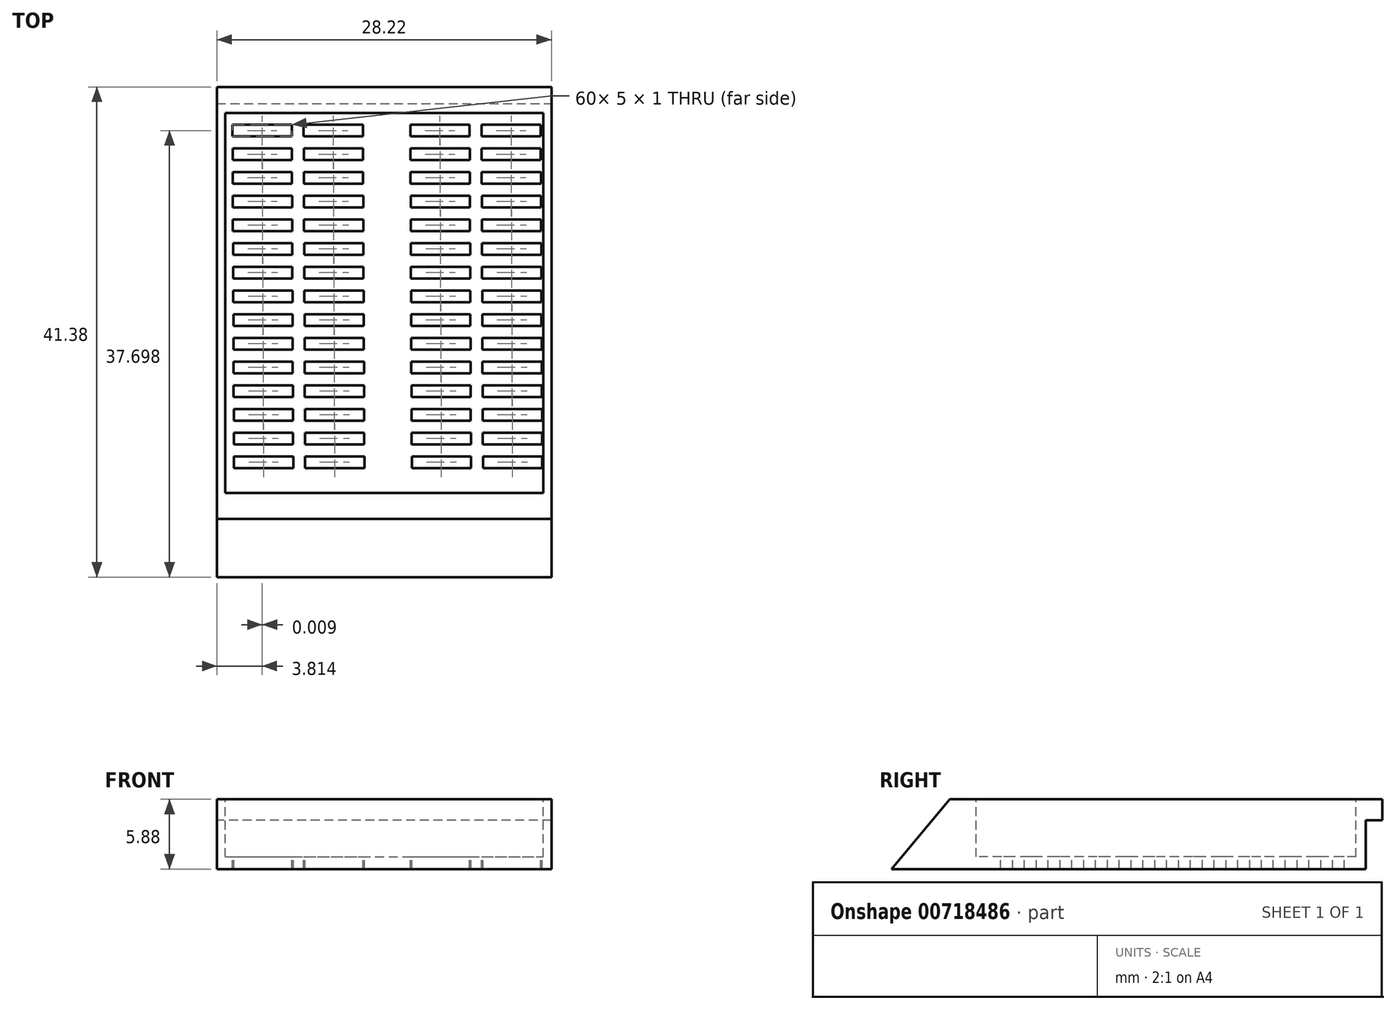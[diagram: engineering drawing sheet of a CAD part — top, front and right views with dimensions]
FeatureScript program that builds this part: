
annotation { "Feature Type Name" : "Feature", "Feature Type Description" : "" }
export const myFeature = defineFeature(function(context is Context, id is Id, definition is map)
    precondition{}
    {
        {
            var Q0;
            Q0=qCreatedBy(makeId("Top.planeOp"),FACE);
            var sketch = newSketch(context, id + "F0", { "sketchPlane" : qUnion([Q0])});
            skLineSegment(sketch, "E0.bottom", {"start": v(-12.14, 10.35) * mm, "end": v(16.08, 10.35) * mm});
            skLineSegment(sketch, "E0.top", {"start": v(-12.14, -29.63) * mm, "end": v(16.08, -29.63) * mm});
            skLineSegment(sketch, "E0.left", {"start": v(-12.14, 10.35) * mm, "end": v(-12.14, -29.63) * mm});
            skLineSegment(sketch, "E0.right", {"start": v(16.08, 10.35) * mm, "end": v(16.08, -29.63) * mm});
            skSolve(sketch);
        }
        {
            var Q0;
            Q0 = qSketchRegion(id + "F0", true);
            extrude(context, id + "F1", {"entities" : qUnion([Q0]), "depth" : 5.88 * mm, "offsetDistance" : 25.4 * mm});
        }
        {
            var Q0;
            Q0=makeQuery(id+"F1.opExtrude","SWEPT_FACE",FACE,{"disambiguationData":[OSD([sQuery(id+"F0.wireOp",EDGE,"E0.left")])]});
            var sketch = newSketch(context, id + "F2", { "sketchPlane" : qUnion([Q0])});
            skLineSegment(sketch, "E1", {"start": v(29.63, 0) * mm, "end": v(24.7, 0) * mm});
            skLineSegment(sketch, "E2", {"start": v(24.7, 0) * mm, "end": v(24.7, 5.88) * mm});
            skLineSegment(sketch, "E3", {"start": v(24.7, 5.88) * mm, "end": v(29.63, 0) * mm});
            skLineSegment(sketch, "E4", {"start": v(29.63, 0) * mm, "end": v(29.63, 5.88) * mm});
            skLineSegment(sketch, "E5", {"start": v(29.63, 5.88) * mm, "end": v(24.7, 5.88) * mm});
            skSolve(sketch);
        }
        {
            var Q0;
            Q0=makeQuery(id+"F2.imprint","IMPRINT",FACE,{"disambiguationData":[TD([[makeQuery(id+"F2.imprint","IMPRINT",EDGE,{"derivedFrom":sQuery(id+"F2.wireOp",EDGE,"E3")}),1.0]])]});
            extrude(context, id + "F3", {"entities" : qUnion([Q0]), "operationType" : NewBodyOperationType.REMOVE, "endBound" : BoundingType.UP_TO_NEXT, "oppositeDirection" : true, "depth" : 25.4 * mm, "offsetDistance" : 25.4 * mm});
        }
        {
            var Q0;
            Q0=makeQuery(id+"F1.opExtrude","SWEPT_FACE",FACE,{"disambiguationData":[OSD([sQuery(id+"F0.wireOp",EDGE,"E0.bottom")])]});
            var sketch = newSketch(context, id + "F4", { "sketchPlane" : qUnion([Q0])});
            skLineSegment(sketch, "E6.bottom", {"start": v(-16.08, 5.88) * mm, "end": v(12.14, 5.88) * mm});
            skLineSegment(sketch, "E6.top", {"start": v(-16.08, 4.13) * mm, "end": v(12.14, 4.13) * mm});
            skLineSegment(sketch, "E6.left", {"start": v(-16.08, 5.88) * mm, "end": v(-16.08, 4.13) * mm});
            skLineSegment(sketch, "E6.right", {"start": v(12.14, 5.88) * mm, "end": v(12.14, 4.13) * mm});
            skSolve(sketch);
        }
        {
            var Q0;
            Q0=makeQuery(id+"F4.imprint","IMPRINT",FACE,{"disambiguationData":[TD([[makeQuery(id+"F4.imprint","IMPRINT",EDGE,{"derivedFrom":sQuery(id+"F4.wireOp",EDGE,"E6.bottom")}),1.0]])]});
            extrude(context, id + "F5", {"entities" : qUnion([Q0]), "operationType" : NewBodyOperationType.ADD, "depth" : 1.4 * mm, "offsetDistance" : 25.4 * mm});
        }
        {
            var Q0;
            Q0=makeQuery(id+"F5.boolean.opBoolean","MERGE",FACE,{"derivedFrom":[makeQuery(id+"F1.opExtrude","CAP_FACE",FACE,{"disambiguationData":[OSD([sQuery(id+"F0.wireOp",EDGE,"E0.bottom"),sQuery(id+"F0.wireOp",EDGE,"E0.top"),sQuery(id+"F0.wireOp",EDGE,"E0.left"),sQuery(id+"F0.wireOp",EDGE,"E0.right")])],"isStart":false}),makeQuery(id+"F5.opExtrude","SWEPT_FACE",FACE,{"disambiguationData":[OSD([sQuery(id+"F4.wireOp",EDGE,"E6.bottom")])]})]});
            var sketch = newSketch(context, id + "F6", { "sketchPlane" : qUnion([Q0])});
            skLineSegment(sketch, "E7.bottom", {"start": v(-11.44, 9.55) * mm, "end": v(15.38, 9.55) * mm});
            skLineSegment(sketch, "E7.top", {"start": v(-11.44, -22.5) * mm, "end": v(15.38, -22.5) * mm});
            skLineSegment(sketch, "E7.left", {"start": v(-11.44, 9.55) * mm, "end": v(-11.44, -22.5) * mm});
            skLineSegment(sketch, "E7.right", {"start": v(15.38, 9.55) * mm, "end": v(15.38, -22.5) * mm});
            skLineSegment(sketch, "E8", {"start": v(-11.44, -6.48) * mm, "end": v(-12.14, -6.48) * mm});
            skLineSegment(sketch, "E9", {"start": v(15.38, -6.48) * mm, "end": v(16.08, -6.48) * mm});
            skLineSegment(sketch, "E10", {"start": v(15.38, -22.5) * mm, "end": v(15.38, -24.7) * mm});
            skLineSegment(sketch, "E11", {"start": v(13.6, 9.55) * mm, "end": v(13.6, 11.75) * mm});
            skSolve(sketch);
        }
        {
            var Q0;
            {var subQ4=sQuery(id+"F6.wireOp",EDGE,"E7.top");Q0=makeQuery(id+"F6.imprint","IMPRINT",FACE,{"disambiguationData":[TD([[makeQuery(id+"F6.imprint","IMPRINT",EDGE,{"derivedFrom":subQ4}),1.0]])]});}
            extrude(context, id + "F7", {"entities" : qUnion([Q0]), "operationType" : NewBodyOperationType.REMOVE, "oppositeDirection" : true, "depth" : 4.85 * mm, "offsetDistance" : 25.4 * mm});
        }
        {
            var Q0;
            {var subQ4=sQuery(id+"F6.wireOp",EDGE,"E7.top");Q0=makeQuery(id+"F6.imprint","IMPRINT",FACE,{"disambiguationData":[TD([[makeQuery(id+"F6.imprint","IMPRINT",EDGE,{"derivedFrom":subQ4}),1.0]])]});}
            var sketch = newSketch(context, id + "F8", { "sketchPlane" : qUnion([Q0])});
            skLineSegment(sketch, "E12.bottom", {"start": v(-10.83, 8.57) * mm, "end": v(-5.83, 8.57) * mm});
            skLineSegment(sketch, "E12.top", {"start": v(-10.83, 7.57) * mm, "end": v(-5.83, 7.57) * mm});
            skLineSegment(sketch, "E12.left", {"start": v(-10.83, 8.57) * mm, "end": v(-10.83, 7.57) * mm});
            skLineSegment(sketch, "E12.right", {"start": v(-5.83, 8.57) * mm, "end": v(-5.83, 7.57) * mm});
            skLineSegment(sketch, "E13", {"start": v(-10.83, 8.57) * mm, "end": v(-10.83, 9.57) * mm});
            skLineSegment(sketch, "E14.1.0.0", {"start": v(-4.83, 8.57) * mm, "end": v(0.17, 8.57) * mm});
            skLineSegment(sketch, "E14.1.0.1", {"start": v(-4.83, 7.57) * mm, "end": v(0.17, 7.57) * mm});
            skLineSegment(sketch, "E14.1.0.2", {"start": v(0.17, 8.57) * mm, "end": v(0.17, 7.57) * mm});
            skLineSegment(sketch, "E14.1.0.3", {"start": v(-4.83, 8.57) * mm, "end": v(-4.83, 7.57) * mm});
            skLineSegment(sketch, "E14.direction1", {"start": v(-10.83, 7.57) * mm, "end": v(-4.83, 7.57) * mm, "construction": true});
            skLineSegment(sketch, "E15.1.0.0", {"start": v(10.17, 8.57) * mm, "end": v(10.17, 7.57) * mm});
            skLineSegment(sketch, "E15.1.0.1", {"start": v(15.17, 8.57) * mm, "end": v(15.17, 7.57) * mm});
            skLineSegment(sketch, "E15.1.0.2", {"start": v(10.17, 7.57) * mm, "end": v(15.17, 7.57) * mm});
            skLineSegment(sketch, "E15.1.0.3", {"start": v(10.17, 8.57) * mm, "end": v(15.17, 8.57) * mm});
            skLineSegment(sketch, "E15.1.0.4", {"start": v(4.17, 8.57) * mm, "end": v(9.17, 8.57) * mm});
            skLineSegment(sketch, "E15.1.0.5", {"start": v(9.17, 8.57) * mm, "end": v(9.17, 7.57) * mm});
            skLineSegment(sketch, "E15.1.0.6", {"start": v(4.17, 7.57) * mm, "end": v(10.17, 7.57) * mm, "construction": true});
            skLineSegment(sketch, "E15.1.0.7", {"start": v(4.17, 8.57) * mm, "end": v(4.17, 7.57) * mm});
            skLineSegment(sketch, "E15.1.0.8", {"start": v(4.17, 7.57) * mm, "end": v(9.17, 7.57) * mm});
            skLineSegment(sketch, "E15.direction1", {"start": v(-10.83, 7.57) * mm, "end": v(4.17, 7.57) * mm, "construction": true});
            skLineSegment(sketch, "E16.1.0.0", {"start": v(4.18, 5.57) * mm, "end": v(10.18, 5.57) * mm, "construction": true});
            skLineSegment(sketch, "E16.1.0.1", {"start": v(-4.82, 6.57) * mm, "end": v(0.18, 6.57) * mm});
            skLineSegment(sketch, "E16.1.0.2", {"start": v(10.18, 6.57) * mm, "end": v(15.18, 6.57) * mm});
            skLineSegment(sketch, "E16.1.0.3", {"start": v(4.18, 6.57) * mm, "end": v(9.18, 6.57) * mm});
            skLineSegment(sketch, "E16.1.0.4", {"start": v(9.18, 6.57) * mm, "end": v(9.18, 5.57) * mm});
            skLineSegment(sketch, "E16.1.0.5", {"start": v(-5.82, 6.57) * mm, "end": v(-5.82, 5.57) * mm});
            skLineSegment(sketch, "E16.1.0.6", {"start": v(-10.82, 6.57) * mm, "end": v(-5.82, 6.57) * mm});
            skLineSegment(sketch, "E16.1.0.7", {"start": v(-10.82, 6.57) * mm, "end": v(-10.82, 5.57) * mm});
            skLineSegment(sketch, "E16.1.0.8", {"start": v(0.18, 6.57) * mm, "end": v(0.18, 5.57) * mm});
            skLineSegment(sketch, "E16.1.0.9", {"start": v(-4.82, 6.57) * mm, "end": v(-4.82, 5.57) * mm});
            skLineSegment(sketch, "E16.1.0.10", {"start": v(10.18, 6.57) * mm, "end": v(10.18, 5.57) * mm});
            skLineSegment(sketch, "E16.1.0.11", {"start": v(4.18, 6.57) * mm, "end": v(4.18, 5.57) * mm});
            skLineSegment(sketch, "E16.1.0.12", {"start": v(15.18, 6.57) * mm, "end": v(15.18, 5.57) * mm});
            skLineSegment(sketch, "E16.1.0.13", {"start": v(10.18, 5.57) * mm, "end": v(15.18, 5.57) * mm});
            skLineSegment(sketch, "E16.1.0.14", {"start": v(-10.82, 5.57) * mm, "end": v(4.18, 5.57) * mm, "construction": true});
            skLineSegment(sketch, "E16.1.0.15", {"start": v(-4.82, 5.57) * mm, "end": v(0.18, 5.57) * mm});
            skLineSegment(sketch, "E16.1.0.16", {"start": v(4.18, 5.57) * mm, "end": v(9.18, 5.57) * mm});
            skLineSegment(sketch, "E16.1.0.17", {"start": v(-10.82, 5.57) * mm, "end": v(-4.82, 5.57) * mm, "construction": true});
            skLineSegment(sketch, "E16.1.0.18", {"start": v(-10.82, 5.57) * mm, "end": v(-5.82, 5.57) * mm});
            skLineSegment(sketch, "E16.2.0.0", {"start": v(4.2, 3.57) * mm, "end": v(10.2, 3.57) * mm, "construction": true});
            skLineSegment(sketch, "E16.2.0.1", {"start": v(-4.8, 4.57) * mm, "end": v(0.2, 4.57) * mm});
            skLineSegment(sketch, "E16.2.0.2", {"start": v(10.2, 4.57) * mm, "end": v(15.2, 4.57) * mm});
            skLineSegment(sketch, "E16.2.0.3", {"start": v(4.2, 4.57) * mm, "end": v(9.2, 4.57) * mm});
            skLineSegment(sketch, "E16.2.0.4", {"start": v(9.2, 4.57) * mm, "end": v(9.2, 3.57) * mm});
            skLineSegment(sketch, "E16.2.0.5", {"start": v(-5.8, 4.57) * mm, "end": v(-5.8, 3.57) * mm});
            skLineSegment(sketch, "E16.2.0.6", {"start": v(-10.8, 4.57) * mm, "end": v(-5.8, 4.57) * mm});
            skLineSegment(sketch, "E16.2.0.7", {"start": v(-10.8, 4.57) * mm, "end": v(-10.8, 3.57) * mm});
            skLineSegment(sketch, "E16.2.0.8", {"start": v(0.2, 4.57) * mm, "end": v(0.2, 3.57) * mm});
            skLineSegment(sketch, "E16.2.0.9", {"start": v(-4.8, 4.57) * mm, "end": v(-4.8, 3.57) * mm});
            skLineSegment(sketch, "E16.2.0.10", {"start": v(10.2, 4.57) * mm, "end": v(10.2, 3.57) * mm});
            skLineSegment(sketch, "E16.2.0.11", {"start": v(4.2, 4.57) * mm, "end": v(4.2, 3.57) * mm});
            skLineSegment(sketch, "E16.2.0.12", {"start": v(15.2, 4.57) * mm, "end": v(15.2, 3.57) * mm});
            skLineSegment(sketch, "E16.2.0.13", {"start": v(10.2, 3.57) * mm, "end": v(15.2, 3.57) * mm});
            skLineSegment(sketch, "E16.2.0.14", {"start": v(-10.8, 3.57) * mm, "end": v(4.2, 3.57) * mm, "construction": true});
            skLineSegment(sketch, "E16.2.0.15", {"start": v(-4.8, 3.57) * mm, "end": v(0.2, 3.57) * mm});
            skLineSegment(sketch, "E16.2.0.16", {"start": v(4.2, 3.57) * mm, "end": v(9.2, 3.57) * mm});
            skLineSegment(sketch, "E16.2.0.17", {"start": v(-10.8, 3.57) * mm, "end": v(-4.8, 3.57) * mm, "construction": true});
            skLineSegment(sketch, "E16.2.0.18", {"start": v(-10.8, 3.57) * mm, "end": v(-5.8, 3.57) * mm});
            skLineSegment(sketch, "E16.3.0.0", {"start": v(4.2, 1.57) * mm, "end": v(10.2, 1.57) * mm, "construction": true});
            skLineSegment(sketch, "E16.3.0.1", {"start": v(-4.8, 2.57) * mm, "end": v(0.2, 2.57) * mm});
            skLineSegment(sketch, "E16.3.0.2", {"start": v(10.2, 2.57) * mm, "end": v(15.2, 2.57) * mm});
            skLineSegment(sketch, "E16.3.0.3", {"start": v(4.2, 2.57) * mm, "end": v(9.2, 2.57) * mm});
            skLineSegment(sketch, "E16.3.0.4", {"start": v(9.2, 2.57) * mm, "end": v(9.2, 1.57) * mm});
            skLineSegment(sketch, "E16.3.0.5", {"start": v(-5.8, 2.57) * mm, "end": v(-5.8, 1.57) * mm});
            skLineSegment(sketch, "E16.3.0.6", {"start": v(-10.8, 2.57) * mm, "end": v(-5.8, 2.57) * mm});
            skLineSegment(sketch, "E16.3.0.7", {"start": v(-10.8, 2.57) * mm, "end": v(-10.8, 1.57) * mm});
            skLineSegment(sketch, "E16.3.0.8", {"start": v(0.2, 2.57) * mm, "end": v(0.2, 1.57) * mm});
            skLineSegment(sketch, "E16.3.0.9", {"start": v(-4.8, 2.57) * mm, "end": v(-4.8, 1.57) * mm});
            skLineSegment(sketch, "E16.3.0.10", {"start": v(10.2, 2.57) * mm, "end": v(10.2, 1.57) * mm});
            skLineSegment(sketch, "E16.3.0.11", {"start": v(4.2, 2.57) * mm, "end": v(4.2, 1.57) * mm});
            skLineSegment(sketch, "E16.3.0.12", {"start": v(15.2, 2.57) * mm, "end": v(15.2, 1.57) * mm});
            skLineSegment(sketch, "E16.3.0.13", {"start": v(10.2, 1.57) * mm, "end": v(15.2, 1.57) * mm});
            skLineSegment(sketch, "E16.3.0.14", {"start": v(-10.8, 1.57) * mm, "end": v(4.2, 1.57) * mm, "construction": true});
            skLineSegment(sketch, "E16.3.0.15", {"start": v(-4.8, 1.57) * mm, "end": v(0.2, 1.57) * mm});
            skLineSegment(sketch, "E16.3.0.16", {"start": v(4.2, 1.57) * mm, "end": v(9.2, 1.57) * mm});
            skLineSegment(sketch, "E16.3.0.17", {"start": v(-10.8, 1.57) * mm, "end": v(-4.8, 1.57) * mm, "construction": true});
            skLineSegment(sketch, "E16.3.0.18", {"start": v(-10.8, 1.57) * mm, "end": v(-5.8, 1.57) * mm});
            skLineSegment(sketch, "E16.4.0.0", {"start": v(4.2, -0.43) * mm, "end": v(10.2, -0.43) * mm, "construction": true});
            skLineSegment(sketch, "E16.4.0.1", {"start": v(-4.8, 0.57) * mm, "end": v(0.2, 0.57) * mm});
            skLineSegment(sketch, "E16.4.0.2", {"start": v(10.2, 0.57) * mm, "end": v(15.2, 0.57) * mm});
            skLineSegment(sketch, "E16.4.0.3", {"start": v(4.2, 0.57) * mm, "end": v(9.2, 0.57) * mm});
            skLineSegment(sketch, "E16.4.0.4", {"start": v(9.2, 0.57) * mm, "end": v(9.2, -0.43) * mm});
            skLineSegment(sketch, "E16.4.0.5", {"start": v(-5.8, 0.57) * mm, "end": v(-5.8, -0.43) * mm});
            skLineSegment(sketch, "E16.4.0.6", {"start": v(-10.8, 0.57) * mm, "end": v(-5.8, 0.57) * mm});
            skLineSegment(sketch, "E16.4.0.7", {"start": v(-10.8, 0.57) * mm, "end": v(-10.8, -0.43) * mm});
            skLineSegment(sketch, "E16.4.0.8", {"start": v(0.2, 0.57) * mm, "end": v(0.2, -0.43) * mm});
            skLineSegment(sketch, "E16.4.0.9", {"start": v(-4.8, 0.57) * mm, "end": v(-4.8, -0.43) * mm});
            skLineSegment(sketch, "E16.4.0.10", {"start": v(10.2, 0.57) * mm, "end": v(10.2, -0.43) * mm});
            skLineSegment(sketch, "E16.4.0.11", {"start": v(4.2, 0.57) * mm, "end": v(4.2, -0.43) * mm});
            skLineSegment(sketch, "E16.4.0.12", {"start": v(15.2, 0.57) * mm, "end": v(15.2, -0.43) * mm});
            skLineSegment(sketch, "E16.4.0.13", {"start": v(10.2, -0.43) * mm, "end": v(15.2, -0.43) * mm});
            skLineSegment(sketch, "E16.4.0.14", {"start": v(-10.8, -0.43) * mm, "end": v(4.2, -0.43) * mm, "construction": true});
            skLineSegment(sketch, "E16.4.0.15", {"start": v(-4.8, -0.43) * mm, "end": v(0.2, -0.43) * mm});
            skLineSegment(sketch, "E16.4.0.16", {"start": v(4.2, -0.43) * mm, "end": v(9.2, -0.43) * mm});
            skLineSegment(sketch, "E16.4.0.17", {"start": v(-10.8, -0.43) * mm, "end": v(-4.8, -0.43) * mm, "construction": true});
            skLineSegment(sketch, "E16.4.0.18", {"start": v(-10.8, -0.43) * mm, "end": v(-5.8, -0.43) * mm});
            skLineSegment(sketch, "E16.5.0.0", {"start": v(4.22, -2.43) * mm, "end": v(10.22, -2.43) * mm, "construction": true});
            skLineSegment(sketch, "E16.5.0.1", {"start": v(-4.78, -1.43) * mm, "end": v(0.22, -1.43) * mm});
            skLineSegment(sketch, "E16.5.0.2", {"start": v(10.22, -1.43) * mm, "end": v(15.22, -1.43) * mm});
            skLineSegment(sketch, "E16.5.0.3", {"start": v(4.22, -1.43) * mm, "end": v(9.22, -1.43) * mm});
            skLineSegment(sketch, "E16.5.0.4", {"start": v(9.22, -1.43) * mm, "end": v(9.22, -2.43) * mm});
            skLineSegment(sketch, "E16.5.0.5", {"start": v(-5.78, -1.43) * mm, "end": v(-5.78, -2.43) * mm});
            skLineSegment(sketch, "E16.5.0.6", {"start": v(-10.78, -1.43) * mm, "end": v(-5.78, -1.43) * mm});
            skLineSegment(sketch, "E16.5.0.7", {"start": v(-10.78, -1.43) * mm, "end": v(-10.78, -2.43) * mm});
            skLineSegment(sketch, "E16.5.0.8", {"start": v(0.22, -1.43) * mm, "end": v(0.22, -2.43) * mm});
            skLineSegment(sketch, "E16.5.0.9", {"start": v(-4.78, -1.43) * mm, "end": v(-4.78, -2.43) * mm});
            skLineSegment(sketch, "E16.5.0.10", {"start": v(10.22, -1.43) * mm, "end": v(10.22, -2.43) * mm});
            skLineSegment(sketch, "E16.5.0.11", {"start": v(4.22, -1.43) * mm, "end": v(4.22, -2.43) * mm});
            skLineSegment(sketch, "E16.5.0.12", {"start": v(15.22, -1.43) * mm, "end": v(15.22, -2.43) * mm});
            skLineSegment(sketch, "E16.5.0.13", {"start": v(10.22, -2.43) * mm, "end": v(15.22, -2.43) * mm});
            skLineSegment(sketch, "E16.5.0.14", {"start": v(-10.78, -2.43) * mm, "end": v(4.22, -2.43) * mm, "construction": true});
            skLineSegment(sketch, "E16.5.0.15", {"start": v(-4.78, -2.43) * mm, "end": v(0.22, -2.43) * mm});
            skLineSegment(sketch, "E16.5.0.16", {"start": v(4.22, -2.43) * mm, "end": v(9.22, -2.43) * mm});
            skLineSegment(sketch, "E16.5.0.17", {"start": v(-10.78, -2.43) * mm, "end": v(-4.78, -2.43) * mm, "construction": true});
            skLineSegment(sketch, "E16.5.0.18", {"start": v(-10.78, -2.43) * mm, "end": v(-5.78, -2.43) * mm});
            skLineSegment(sketch, "E16.6.0.0", {"start": v(4.23, -4.43) * mm, "end": v(10.23, -4.43) * mm, "construction": true});
            skLineSegment(sketch, "E16.6.0.1", {"start": v(-4.77, -3.43) * mm, "end": v(0.23, -3.43) * mm});
            skLineSegment(sketch, "E16.6.0.2", {"start": v(10.23, -3.43) * mm, "end": v(15.23, -3.43) * mm});
            skLineSegment(sketch, "E16.6.0.3", {"start": v(4.23, -3.43) * mm, "end": v(9.23, -3.43) * mm});
            skLineSegment(sketch, "E16.6.0.4", {"start": v(9.23, -3.43) * mm, "end": v(9.23, -4.43) * mm});
            skLineSegment(sketch, "E16.6.0.5", {"start": v(-5.77, -3.43) * mm, "end": v(-5.77, -4.43) * mm});
            skLineSegment(sketch, "E16.6.0.6", {"start": v(-10.77, -3.43) * mm, "end": v(-5.77, -3.43) * mm});
            skLineSegment(sketch, "E16.6.0.7", {"start": v(-10.77, -3.43) * mm, "end": v(-10.77, -4.43) * mm});
            skLineSegment(sketch, "E16.6.0.8", {"start": v(0.23, -3.43) * mm, "end": v(0.23, -4.43) * mm});
            skLineSegment(sketch, "E16.6.0.9", {"start": v(-4.77, -3.43) * mm, "end": v(-4.77, -4.43) * mm});
            skLineSegment(sketch, "E16.6.0.10", {"start": v(10.23, -3.43) * mm, "end": v(10.23, -4.43) * mm});
            skLineSegment(sketch, "E16.6.0.11", {"start": v(4.23, -3.43) * mm, "end": v(4.23, -4.43) * mm});
            skLineSegment(sketch, "E16.6.0.12", {"start": v(15.23, -3.43) * mm, "end": v(15.23, -4.43) * mm});
            skLineSegment(sketch, "E16.6.0.13", {"start": v(10.23, -4.43) * mm, "end": v(15.23, -4.43) * mm});
            skLineSegment(sketch, "E16.6.0.14", {"start": v(-10.77, -4.43) * mm, "end": v(4.23, -4.43) * mm, "construction": true});
            skLineSegment(sketch, "E16.6.0.15", {"start": v(-4.77, -4.43) * mm, "end": v(0.23, -4.43) * mm});
            skLineSegment(sketch, "E16.6.0.16", {"start": v(4.23, -4.43) * mm, "end": v(9.23, -4.43) * mm});
            skLineSegment(sketch, "E16.6.0.17", {"start": v(-10.77, -4.43) * mm, "end": v(-4.77, -4.43) * mm, "construction": true});
            skLineSegment(sketch, "E16.6.0.18", {"start": v(-10.77, -4.43) * mm, "end": v(-5.77, -4.43) * mm});
            skLineSegment(sketch, "E16.7.0.0", {"start": v(4.23, -6.43) * mm, "end": v(10.23, -6.43) * mm, "construction": true});
            skLineSegment(sketch, "E16.7.0.1", {"start": v(-4.77, -5.43) * mm, "end": v(0.23, -5.43) * mm});
            skLineSegment(sketch, "E16.7.0.2", {"start": v(10.23, -5.43) * mm, "end": v(15.23, -5.43) * mm});
            skLineSegment(sketch, "E16.7.0.3", {"start": v(4.23, -5.43) * mm, "end": v(9.23, -5.43) * mm});
            skLineSegment(sketch, "E16.7.0.4", {"start": v(9.23, -5.43) * mm, "end": v(9.23, -6.43) * mm});
            skLineSegment(sketch, "E16.7.0.5", {"start": v(-5.77, -5.43) * mm, "end": v(-5.77, -6.43) * mm});
            skLineSegment(sketch, "E16.7.0.6", {"start": v(-10.77, -5.43) * mm, "end": v(-5.77, -5.43) * mm});
            skLineSegment(sketch, "E16.7.0.7", {"start": v(-10.77, -5.43) * mm, "end": v(-10.77, -6.43) * mm});
            skLineSegment(sketch, "E16.7.0.8", {"start": v(0.23, -5.43) * mm, "end": v(0.23, -6.43) * mm});
            skLineSegment(sketch, "E16.7.0.9", {"start": v(-4.77, -5.43) * mm, "end": v(-4.77, -6.43) * mm});
            skLineSegment(sketch, "E16.7.0.10", {"start": v(10.23, -5.43) * mm, "end": v(10.23, -6.43) * mm});
            skLineSegment(sketch, "E16.7.0.11", {"start": v(4.23, -5.43) * mm, "end": v(4.23, -6.43) * mm});
            skLineSegment(sketch, "E16.7.0.12", {"start": v(15.23, -5.43) * mm, "end": v(15.23, -6.43) * mm});
            skLineSegment(sketch, "E16.7.0.13", {"start": v(10.23, -6.43) * mm, "end": v(15.23, -6.43) * mm});
            skLineSegment(sketch, "E16.7.0.14", {"start": v(-10.77, -6.43) * mm, "end": v(4.23, -6.43) * mm, "construction": true});
            skLineSegment(sketch, "E16.7.0.15", {"start": v(-4.77, -6.43) * mm, "end": v(0.23, -6.43) * mm});
            skLineSegment(sketch, "E16.7.0.16", {"start": v(4.23, -6.43) * mm, "end": v(9.23, -6.43) * mm});
            skLineSegment(sketch, "E16.7.0.17", {"start": v(-10.77, -6.43) * mm, "end": v(-4.77, -6.43) * mm, "construction": true});
            skLineSegment(sketch, "E16.7.0.18", {"start": v(-10.77, -6.43) * mm, "end": v(-5.77, -6.43) * mm});
            skLineSegment(sketch, "E16.8.0.0", {"start": v(4.24, -8.43) * mm, "end": v(10.24, -8.43) * mm, "construction": true});
            skLineSegment(sketch, "E16.8.0.1", {"start": v(-4.76, -7.43) * mm, "end": v(0.24, -7.43) * mm});
            skLineSegment(sketch, "E16.8.0.2", {"start": v(10.24, -7.43) * mm, "end": v(15.24, -7.43) * mm});
            skLineSegment(sketch, "E16.8.0.3", {"start": v(4.24, -7.43) * mm, "end": v(9.24, -7.43) * mm});
            skLineSegment(sketch, "E16.8.0.4", {"start": v(9.24, -7.43) * mm, "end": v(9.24, -8.43) * mm});
            skLineSegment(sketch, "E16.8.0.5", {"start": v(-5.76, -7.43) * mm, "end": v(-5.76, -8.43) * mm});
            skLineSegment(sketch, "E16.8.0.6", {"start": v(-10.76, -7.43) * mm, "end": v(-5.76, -7.43) * mm});
            skLineSegment(sketch, "E16.8.0.7", {"start": v(-10.76, -7.43) * mm, "end": v(-10.76, -8.43) * mm});
            skLineSegment(sketch, "E16.8.0.8", {"start": v(0.24, -7.43) * mm, "end": v(0.24, -8.43) * mm});
            skLineSegment(sketch, "E16.8.0.9", {"start": v(-4.76, -7.43) * mm, "end": v(-4.76, -8.43) * mm});
            skLineSegment(sketch, "E16.8.0.10", {"start": v(10.24, -7.43) * mm, "end": v(10.24, -8.43) * mm});
            skLineSegment(sketch, "E16.8.0.11", {"start": v(4.24, -7.43) * mm, "end": v(4.24, -8.43) * mm});
            skLineSegment(sketch, "E16.8.0.12", {"start": v(15.24, -7.43) * mm, "end": v(15.24, -8.43) * mm});
            skLineSegment(sketch, "E16.8.0.13", {"start": v(10.24, -8.43) * mm, "end": v(15.24, -8.43) * mm});
            skLineSegment(sketch, "E16.8.0.14", {"start": v(-10.76, -8.43) * mm, "end": v(4.24, -8.43) * mm, "construction": true});
            skLineSegment(sketch, "E16.8.0.15", {"start": v(-4.76, -8.43) * mm, "end": v(0.24, -8.43) * mm});
            skLineSegment(sketch, "E16.8.0.16", {"start": v(4.24, -8.43) * mm, "end": v(9.24, -8.43) * mm});
            skLineSegment(sketch, "E16.8.0.17", {"start": v(-10.76, -8.43) * mm, "end": v(-4.76, -8.43) * mm, "construction": true});
            skLineSegment(sketch, "E16.8.0.18", {"start": v(-10.76, -8.43) * mm, "end": v(-5.76, -8.43) * mm});
            skLineSegment(sketch, "E16.9.0.0", {"start": v(4.25, -10.43) * mm, "end": v(10.25, -10.43) * mm, "construction": true});
            skLineSegment(sketch, "E16.9.0.1", {"start": v(-4.75, -9.43) * mm, "end": v(0.25, -9.43) * mm});
            skLineSegment(sketch, "E16.9.0.2", {"start": v(10.25, -9.43) * mm, "end": v(15.25, -9.43) * mm});
            skLineSegment(sketch, "E16.9.0.3", {"start": v(4.25, -9.43) * mm, "end": v(9.25, -9.43) * mm});
            skLineSegment(sketch, "E16.9.0.4", {"start": v(9.25, -9.43) * mm, "end": v(9.25, -10.43) * mm});
            skLineSegment(sketch, "E16.9.0.5", {"start": v(-5.75, -9.43) * mm, "end": v(-5.75, -10.43) * mm});
            skLineSegment(sketch, "E16.9.0.6", {"start": v(-10.75, -9.43) * mm, "end": v(-5.75, -9.43) * mm});
            skLineSegment(sketch, "E16.9.0.7", {"start": v(-10.75, -9.43) * mm, "end": v(-10.75, -10.43) * mm});
            skLineSegment(sketch, "E16.9.0.8", {"start": v(0.25, -9.43) * mm, "end": v(0.25, -10.43) * mm});
            skLineSegment(sketch, "E16.9.0.9", {"start": v(-4.75, -9.43) * mm, "end": v(-4.75, -10.43) * mm});
            skLineSegment(sketch, "E16.9.0.10", {"start": v(10.25, -9.43) * mm, "end": v(10.25, -10.43) * mm});
            skLineSegment(sketch, "E16.9.0.11", {"start": v(4.25, -9.43) * mm, "end": v(4.25, -10.43) * mm});
            skLineSegment(sketch, "E16.9.0.12", {"start": v(15.25, -9.43) * mm, "end": v(15.25, -10.43) * mm});
            skLineSegment(sketch, "E16.9.0.13", {"start": v(10.25, -10.43) * mm, "end": v(15.25, -10.43) * mm});
            skLineSegment(sketch, "E16.9.0.14", {"start": v(-10.75, -10.43) * mm, "end": v(4.25, -10.43) * mm, "construction": true});
            skLineSegment(sketch, "E16.9.0.15", {"start": v(-4.75, -10.43) * mm, "end": v(0.25, -10.43) * mm});
            skLineSegment(sketch, "E16.9.0.16", {"start": v(4.25, -10.43) * mm, "end": v(9.25, -10.43) * mm});
            skLineSegment(sketch, "E16.9.0.17", {"start": v(-10.75, -10.43) * mm, "end": v(-4.75, -10.43) * mm, "construction": true});
            skLineSegment(sketch, "E16.9.0.18", {"start": v(-10.75, -10.43) * mm, "end": v(-5.75, -10.43) * mm});
            skLineSegment(sketch, "E16.10.0.0", {"start": v(4.26, -12.43) * mm, "end": v(10.26, -12.43) * mm, "construction": true});
            skLineSegment(sketch, "E16.10.0.1", {"start": v(-4.74, -11.43) * mm, "end": v(0.26, -11.43) * mm});
            skLineSegment(sketch, "E16.10.0.2", {"start": v(10.26, -11.43) * mm, "end": v(15.26, -11.43) * mm});
            skLineSegment(sketch, "E16.10.0.3", {"start": v(4.26, -11.43) * mm, "end": v(9.26, -11.43) * mm});
            skLineSegment(sketch, "E16.10.0.4", {"start": v(9.26, -11.43) * mm, "end": v(9.26, -12.43) * mm});
            skLineSegment(sketch, "E16.10.0.5", {"start": v(-5.74, -11.43) * mm, "end": v(-5.74, -12.43) * mm});
            skLineSegment(sketch, "E16.10.0.6", {"start": v(-10.74, -11.43) * mm, "end": v(-5.74, -11.43) * mm});
            skLineSegment(sketch, "E16.10.0.7", {"start": v(-10.74, -11.43) * mm, "end": v(-10.74, -12.43) * mm});
            skLineSegment(sketch, "E16.10.0.8", {"start": v(0.26, -11.43) * mm, "end": v(0.26, -12.43) * mm});
            skLineSegment(sketch, "E16.10.0.9", {"start": v(-4.74, -11.43) * mm, "end": v(-4.74, -12.43) * mm});
            skLineSegment(sketch, "E16.10.0.10", {"start": v(10.26, -11.43) * mm, "end": v(10.26, -12.43) * mm});
            skLineSegment(sketch, "E16.10.0.11", {"start": v(4.26, -11.43) * mm, "end": v(4.26, -12.43) * mm});
            skLineSegment(sketch, "E16.10.0.12", {"start": v(15.26, -11.43) * mm, "end": v(15.26, -12.43) * mm});
            skLineSegment(sketch, "E16.10.0.13", {"start": v(10.26, -12.43) * mm, "end": v(15.26, -12.43) * mm});
            skLineSegment(sketch, "E16.10.0.14", {"start": v(-10.74, -12.43) * mm, "end": v(4.26, -12.43) * mm, "construction": true});
            skLineSegment(sketch, "E16.10.0.15", {"start": v(-4.74, -12.43) * mm, "end": v(0.26, -12.43) * mm});
            skLineSegment(sketch, "E16.10.0.16", {"start": v(4.26, -12.43) * mm, "end": v(9.26, -12.43) * mm});
            skLineSegment(sketch, "E16.10.0.17", {"start": v(-10.74, -12.43) * mm, "end": v(-4.74, -12.43) * mm, "construction": true});
            skLineSegment(sketch, "E16.10.0.18", {"start": v(-10.74, -12.43) * mm, "end": v(-5.74, -12.43) * mm});
            skLineSegment(sketch, "E16.11.0.0", {"start": v(4.27, -14.43) * mm, "end": v(10.27, -14.43) * mm, "construction": true});
            skLineSegment(sketch, "E16.11.0.1", {"start": v(-4.73, -13.43) * mm, "end": v(0.27, -13.43) * mm});
            skLineSegment(sketch, "E16.11.0.2", {"start": v(10.27, -13.43) * mm, "end": v(15.27, -13.43) * mm});
            skLineSegment(sketch, "E16.11.0.3", {"start": v(4.27, -13.43) * mm, "end": v(9.27, -13.43) * mm});
            skLineSegment(sketch, "E16.11.0.4", {"start": v(9.27, -13.43) * mm, "end": v(9.27, -14.43) * mm});
            skLineSegment(sketch, "E16.11.0.5", {"start": v(-5.73, -13.43) * mm, "end": v(-5.73, -14.43) * mm});
            skLineSegment(sketch, "E16.11.0.6", {"start": v(-10.73, -13.43) * mm, "end": v(-5.73, -13.43) * mm});
            skLineSegment(sketch, "E16.11.0.7", {"start": v(-10.73, -13.43) * mm, "end": v(-10.73, -14.43) * mm});
            skLineSegment(sketch, "E16.11.0.8", {"start": v(0.27, -13.43) * mm, "end": v(0.27, -14.43) * mm});
            skLineSegment(sketch, "E16.11.0.9", {"start": v(-4.73, -13.43) * mm, "end": v(-4.73, -14.43) * mm});
            skLineSegment(sketch, "E16.11.0.10", {"start": v(10.27, -13.43) * mm, "end": v(10.27, -14.43) * mm});
            skLineSegment(sketch, "E16.11.0.11", {"start": v(4.27, -13.43) * mm, "end": v(4.27, -14.43) * mm});
            skLineSegment(sketch, "E16.11.0.12", {"start": v(15.27, -13.43) * mm, "end": v(15.27, -14.43) * mm});
            skLineSegment(sketch, "E16.11.0.13", {"start": v(10.27, -14.43) * mm, "end": v(15.27, -14.43) * mm});
            skLineSegment(sketch, "E16.11.0.14", {"start": v(-10.73, -14.43) * mm, "end": v(4.27, -14.43) * mm, "construction": true});
            skLineSegment(sketch, "E16.11.0.15", {"start": v(-4.73, -14.43) * mm, "end": v(0.27, -14.43) * mm});
            skLineSegment(sketch, "E16.11.0.16", {"start": v(4.27, -14.43) * mm, "end": v(9.27, -14.43) * mm});
            skLineSegment(sketch, "E16.11.0.17", {"start": v(-10.73, -14.43) * mm, "end": v(-4.73, -14.43) * mm, "construction": true});
            skLineSegment(sketch, "E16.11.0.18", {"start": v(-10.73, -14.43) * mm, "end": v(-5.73, -14.43) * mm});
            skLineSegment(sketch, "E16.12.0.0", {"start": v(4.28, -16.43) * mm, "end": v(10.28, -16.43) * mm, "construction": true});
            skLineSegment(sketch, "E16.12.0.1", {"start": v(-4.72, -15.43) * mm, "end": v(0.28, -15.43) * mm});
            skLineSegment(sketch, "E16.12.0.2", {"start": v(10.28, -15.43) * mm, "end": v(15.28, -15.43) * mm});
            skLineSegment(sketch, "E16.12.0.3", {"start": v(4.28, -15.43) * mm, "end": v(9.28, -15.43) * mm});
            skLineSegment(sketch, "E16.12.0.4", {"start": v(9.28, -15.43) * mm, "end": v(9.28, -16.43) * mm});
            skLineSegment(sketch, "E16.12.0.5", {"start": v(-5.72, -15.43) * mm, "end": v(-5.72, -16.43) * mm});
            skLineSegment(sketch, "E16.12.0.6", {"start": v(-10.72, -15.43) * mm, "end": v(-5.72, -15.43) * mm});
            skLineSegment(sketch, "E16.12.0.7", {"start": v(-10.72, -15.43) * mm, "end": v(-10.72, -16.43) * mm});
            skLineSegment(sketch, "E16.12.0.8", {"start": v(0.28, -15.43) * mm, "end": v(0.28, -16.43) * mm});
            skLineSegment(sketch, "E16.12.0.9", {"start": v(-4.72, -15.43) * mm, "end": v(-4.72, -16.43) * mm});
            skLineSegment(sketch, "E16.12.0.10", {"start": v(10.28, -15.43) * mm, "end": v(10.28, -16.43) * mm});
            skLineSegment(sketch, "E16.12.0.11", {"start": v(4.28, -15.43) * mm, "end": v(4.28, -16.43) * mm});
            skLineSegment(sketch, "E16.12.0.12", {"start": v(15.28, -15.43) * mm, "end": v(15.28, -16.43) * mm});
            skLineSegment(sketch, "E16.12.0.13", {"start": v(10.28, -16.43) * mm, "end": v(15.28, -16.43) * mm});
            skLineSegment(sketch, "E16.12.0.14", {"start": v(-10.72, -16.43) * mm, "end": v(4.28, -16.43) * mm, "construction": true});
            skLineSegment(sketch, "E16.12.0.15", {"start": v(-4.72, -16.43) * mm, "end": v(0.28, -16.43) * mm});
            skLineSegment(sketch, "E16.12.0.16", {"start": v(4.28, -16.43) * mm, "end": v(9.28, -16.43) * mm});
            skLineSegment(sketch, "E16.12.0.17", {"start": v(-10.72, -16.43) * mm, "end": v(-4.72, -16.43) * mm, "construction": true});
            skLineSegment(sketch, "E16.12.0.18", {"start": v(-10.72, -16.43) * mm, "end": v(-5.72, -16.43) * mm});
            skLineSegment(sketch, "E16.13.0.0", {"start": v(4.29, -18.43) * mm, "end": v(10.29, -18.43) * mm, "construction": true});
            skLineSegment(sketch, "E16.13.0.1", {"start": v(-4.71, -17.43) * mm, "end": v(0.29, -17.43) * mm});
            skLineSegment(sketch, "E16.13.0.2", {"start": v(10.29, -17.43) * mm, "end": v(15.29, -17.43) * mm});
            skLineSegment(sketch, "E16.13.0.3", {"start": v(4.29, -17.43) * mm, "end": v(9.29, -17.43) * mm});
            skLineSegment(sketch, "E16.13.0.4", {"start": v(9.29, -17.43) * mm, "end": v(9.29, -18.43) * mm});
            skLineSegment(sketch, "E16.13.0.5", {"start": v(-5.71, -17.43) * mm, "end": v(-5.71, -18.43) * mm});
            skLineSegment(sketch, "E16.13.0.6", {"start": v(-10.71, -17.43) * mm, "end": v(-5.71, -17.43) * mm});
            skLineSegment(sketch, "E16.13.0.7", {"start": v(-10.71, -17.43) * mm, "end": v(-10.71, -18.43) * mm});
            skLineSegment(sketch, "E16.13.0.8", {"start": v(0.29, -17.43) * mm, "end": v(0.29, -18.43) * mm});
            skLineSegment(sketch, "E16.13.0.9", {"start": v(-4.71, -17.43) * mm, "end": v(-4.71, -18.43) * mm});
            skLineSegment(sketch, "E16.13.0.10", {"start": v(10.29, -17.43) * mm, "end": v(10.29, -18.43) * mm});
            skLineSegment(sketch, "E16.13.0.11", {"start": v(4.29, -17.43) * mm, "end": v(4.29, -18.43) * mm});
            skLineSegment(sketch, "E16.13.0.12", {"start": v(15.29, -17.43) * mm, "end": v(15.29, -18.43) * mm});
            skLineSegment(sketch, "E16.13.0.13", {"start": v(10.29, -18.43) * mm, "end": v(15.29, -18.43) * mm});
            skLineSegment(sketch, "E16.13.0.14", {"start": v(-10.71, -18.43) * mm, "end": v(4.29, -18.43) * mm, "construction": true});
            skLineSegment(sketch, "E16.13.0.15", {"start": v(-4.71, -18.43) * mm, "end": v(0.29, -18.43) * mm});
            skLineSegment(sketch, "E16.13.0.16", {"start": v(4.29, -18.43) * mm, "end": v(9.29, -18.43) * mm});
            skLineSegment(sketch, "E16.13.0.17", {"start": v(-10.71, -18.43) * mm, "end": v(-4.71, -18.43) * mm, "construction": true});
            skLineSegment(sketch, "E16.13.0.18", {"start": v(-10.71, -18.43) * mm, "end": v(-5.71, -18.43) * mm});
            skLineSegment(sketch, "E16.14.0.0", {"start": v(4.3, -20.43) * mm, "end": v(10.3, -20.43) * mm, "construction": true});
            skLineSegment(sketch, "E16.14.0.1", {"start": v(-4.7, -19.43) * mm, "end": v(0.3, -19.43) * mm});
            skLineSegment(sketch, "E16.14.0.2", {"start": v(10.3, -19.43) * mm, "end": v(15.3, -19.43) * mm});
            skLineSegment(sketch, "E16.14.0.3", {"start": v(4.3, -19.43) * mm, "end": v(9.3, -19.43) * mm});
            skLineSegment(sketch, "E16.14.0.4", {"start": v(9.3, -19.43) * mm, "end": v(9.3, -20.43) * mm});
            skLineSegment(sketch, "E16.14.0.5", {"start": v(-5.7, -19.43) * mm, "end": v(-5.7, -20.43) * mm});
            skLineSegment(sketch, "E16.14.0.6", {"start": v(-10.7, -19.43) * mm, "end": v(-5.7, -19.43) * mm});
            skLineSegment(sketch, "E16.14.0.7", {"start": v(-10.7, -19.43) * mm, "end": v(-10.7, -20.43) * mm});
            skLineSegment(sketch, "E16.14.0.8", {"start": v(0.3, -19.43) * mm, "end": v(0.3, -20.43) * mm});
            skLineSegment(sketch, "E16.14.0.9", {"start": v(-4.7, -19.43) * mm, "end": v(-4.7, -20.43) * mm});
            skLineSegment(sketch, "E16.14.0.10", {"start": v(10.3, -19.43) * mm, "end": v(10.3, -20.43) * mm});
            skLineSegment(sketch, "E16.14.0.11", {"start": v(4.3, -19.43) * mm, "end": v(4.3, -20.43) * mm});
            skLineSegment(sketch, "E16.14.0.12", {"start": v(15.3, -19.43) * mm, "end": v(15.3, -20.43) * mm});
            skLineSegment(sketch, "E16.14.0.13", {"start": v(10.3, -20.43) * mm, "end": v(15.3, -20.43) * mm});
            skLineSegment(sketch, "E16.14.0.14", {"start": v(-10.7, -20.43) * mm, "end": v(4.3, -20.43) * mm, "construction": true});
            skLineSegment(sketch, "E16.14.0.15", {"start": v(-4.7, -20.43) * mm, "end": v(0.3, -20.43) * mm});
            skLineSegment(sketch, "E16.14.0.16", {"start": v(4.3, -20.43) * mm, "end": v(9.3, -20.43) * mm});
            skLineSegment(sketch, "E16.14.0.17", {"start": v(-10.7, -20.43) * mm, "end": v(-4.7, -20.43) * mm, "construction": true});
            skLineSegment(sketch, "E16.14.0.18", {"start": v(-10.7, -20.43) * mm, "end": v(-5.7, -20.43) * mm});
            skLineSegment(sketch, "E16.direction1", {"start": v(-10.83, 7.57) * mm, "end": v(-10.82, 5.57) * mm, "construction": true});
            skSolve(sketch);
        }
        {
            var Q0;
            Q0 = qSketchRegion(id + "F8", true);
            extrude(context, id + "F9", {"entities" : qUnion([Q0]), "operationType" : NewBodyOperationType.REMOVE, "oppositeDirection" : true, "depth" : 25.4 * mm, "offsetDistance" : 25.4 * mm});
        }
    });
